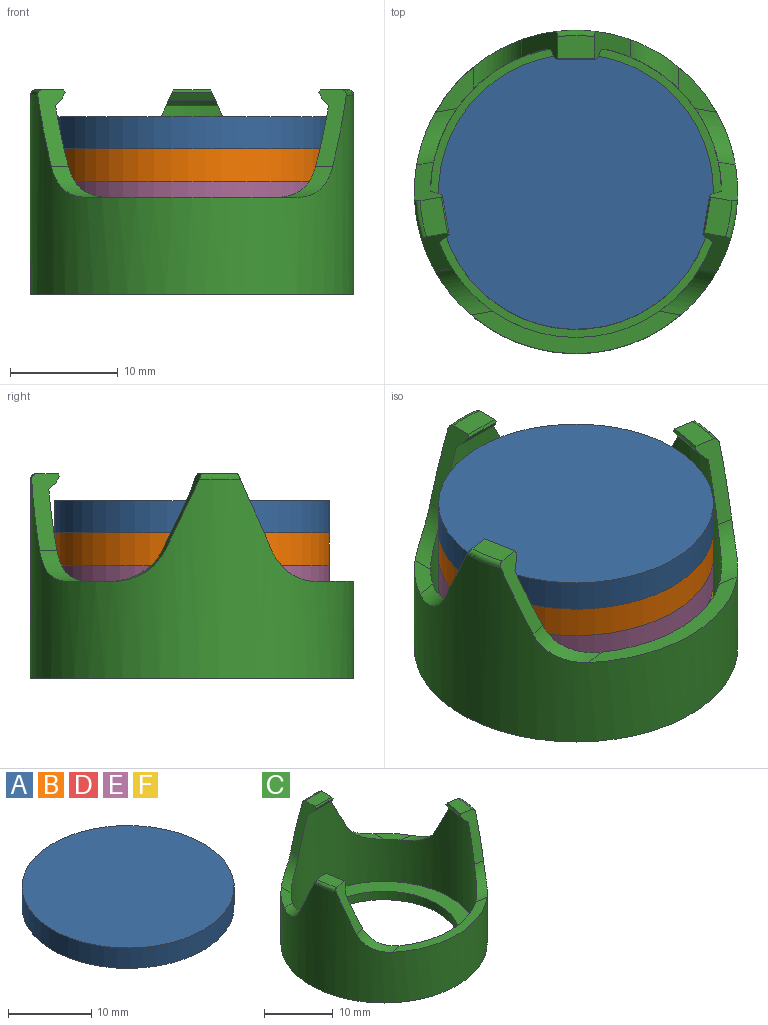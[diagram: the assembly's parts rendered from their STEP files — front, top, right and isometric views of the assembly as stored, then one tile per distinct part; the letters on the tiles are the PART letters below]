
ASSEMBLY  parts=6 mates=5
PART A: 3 faces, bbox 25.5x25.5x3 mm
  f0: cylinder r=12.75mm len=25.5mm, axis (0,0,-1), area 240.3mm2, adj f1,f2
  f1: plane 25.5x25.5mm, normal (0,0,1), area 510.7mm2, adj f0
  f2: plane 25.5x25.5mm, normal (0,0,-1), area 510.7mm2, adj f0
PART B: same geometry as A
PART C: 38 faces, bbox 31.2x30.2x19.1 mm
  f0: cylinder r=13.5mm len=27mm, axis (0,0,-1), area 877.2mm2, adj f5,f8,f9,f10,f11,f12,f13,f14
  f1: cylinder r=15mm len=30mm, axis (0,0,-1), area 1101.1mm2, adj f7,f8,f9,f10,f11,f12,f13,f14
  f2: plane 3.7x2.56mm, normal (0,0,1), area 7mm2, adj f13,f15,f21,f30
  f3: plane 3.7x2.56mm, normal (0,0,1), area 7mm2, adj f10,f12,f25,f29
  f4: plane 3.4x2.1mm, normal (0,0,1), area 7mm2, adj f9,f16,f17,f31
  f5: plane 27x27mm, normal (0,0,1), area 192.4mm2, adj f0,f6
  f6: cylinder r=11mm len=22mm, axis (0,0,-1), area 103.7mm2, adj f5,f7
  f7: plane 30x30mm, normal (0,0,-1), area 326.7mm2, adj f1,f6
  f8: plane 4.17x3.5mm, normal (0,0,1), area 5.9mm2, adj f0,f1,f36,f37
  f9: plane 7.2x3.4mm, normal (0.91,0,0.42), area 13.2mm2, adj f0,f1,f4,f17,f18,f19,f20,f31
  f10: plane 7.2x3.69mm, normal (0.16,0.89,0.42), area 13.2mm2, adj f0,f1,f3,f25,f26,f27,f28,f29
  f11: plane 19.47x3.94mm, normal (0,0,1), area 28.3mm2, adj f0,f1,f32,f33
  f12: plane 7.2x3.65mm, normal (-0.16,-0.89,0.42), area 13.2mm2, adj f0,f1,f3,f25,f26,f27,f28,f29
  f13: plane 7.2x3.65mm, normal (0.16,-0.89,0.42), area 13.2mm2, adj f0,f1,f2,f21,f22,f23,f24,f30
  f14: plane 4.17x3.5mm, normal (0,0,1), area 5.9mm2, adj f0,f1,f34,f35
  f15: plane 7.2x3.69mm, normal (-0.16,0.89,0.42), area 13.2mm2, adj f0,f1,f2,f21,f22,f23,f24,f30
  f16: plane 7.2x3.4mm, normal (-0.91,0,0.42), area 13.2mm2, adj f0,f1,f4,f17,f18,f19,f20,f31
  f17: plane 3.66x0.28mm, normal (0,-0.91,0.42), area 1.1mm2, adj f4,f9,f16,f20
  f18: plane 4.33x0.25mm, normal (0,0,-1), area 0.8mm2, adj f9,f16,f19,f20
  f19: cone r=13.5mm half-angle=45deg, axis (0,0,-1), area 3.3mm2, adj f0,f9,f16,f18
  f20: plane 4.33x0.73mm, normal (0,-0.84,-0.54), area 3.4mm2, adj f9,f16,f17,f18
  f21: plane 3.6x0.74mm, normal (0.89,0.16,0.42), area 1.1mm2, adj f2,f13,f15,f24
  f22: plane 4.28x0.82mm, normal (0,0,-1), area 0.8mm2, adj f13,f15,f23,f24
  f23: cone r=13.5mm half-angle=45deg, axis (0,0,-1), area 3.3mm2, adj f0,f13,f15,f22
  f24: plane 4.27x1.15mm, normal (0.83,0.15,-0.54), area 3.4mm2, adj f13,f15,f21,f22
  f25: plane 3.6x0.74mm, normal (-0.89,0.16,0.42), area 1.1mm2, adj f3,f10,f12,f28
  f26: plane 4.28x0.82mm, normal (0,0,-1), area 0.8mm2, adj f10,f12,f27,f28
  f27: cone r=13.5mm half-angle=45deg, axis (0,0,-1), area 3.3mm2, adj f0,f10,f12,f26
  f28: plane 4.27x1.15mm, normal (-0.83,0.15,-0.54), area 3.4mm2, adj f10,f12,f25,f26
  f29: torus R=14.5mm, axis (0,0,1), area 2.8mm2, adj f1,f3,f10,f12
  f30: torus R=14.5mm, axis (0,0,1), area 2.8mm2, adj f1,f2,f13,f15
  f31: torus R=14.5mm, axis (0,0,1), area 2.8mm2, adj f1,f4,f9,f16
  f32: cylinder r=5mm len=5.31mm, axis (0.98,-0.17,0), area 9.9mm2, adj f0,f1,f11,f12
  f33: cylinder r=5mm len=5.31mm, axis (-0.98,-0.17,0), area 9.9mm2, adj f0,f1,f11,f13
  f34: cylinder r=5mm len=4.59mm, axis (0,1,0), area 9.9mm2, adj f0,f1,f14,f16
  f35: cylinder r=5mm len=5.31mm, axis (-0.98,-0.17,0), area 9.9mm2, adj f0,f1,f14,f15
  f36: cylinder r=5mm len=5.31mm, axis (0.98,-0.17,0), area 9.9mm2, adj f0,f1,f8,f10
  f37: cylinder r=5mm len=4.59mm, axis (0,1,0), area 9.9mm2, adj f0,f1,f8,f9
PART D: same geometry as A
PART E: same geometry as A
PART F: same geometry as A
PLACE A t=(0.04,0.02,3.97)mm
PLACE B t=(0.04,0.02,0.97)mm
PLACE C t=(0.04,0.02,-9.53)mm
PLACE D t=(0.04,0.02,-8.03)mm
PLACE E t=(0.04,0.02,-2.03)mm
PLACE F t=(0.04,0.02,-5.03)mm
MATE cylindrical D.f0 <-> C.f0  axis (0,0,-1) through (0.04,0.02,-8.03)mm
MATE cylindrical E.f0 <-> F.f0  axis (0,0,-1) through (0.04,0.02,-2.03)mm
MATE cylindrical B.f0 <-> E.f0  axis (0,0,-1) through (0.04,0.02,0.97)mm
MATE cylindrical F.f0 <-> D.f0  axis (0,0,-1) through (0.04,0.02,-5.03)mm
MATE cylindrical A.f0 <-> B.f0  axis (0,0,-1) through (0.04,0.02,3.97)mm
